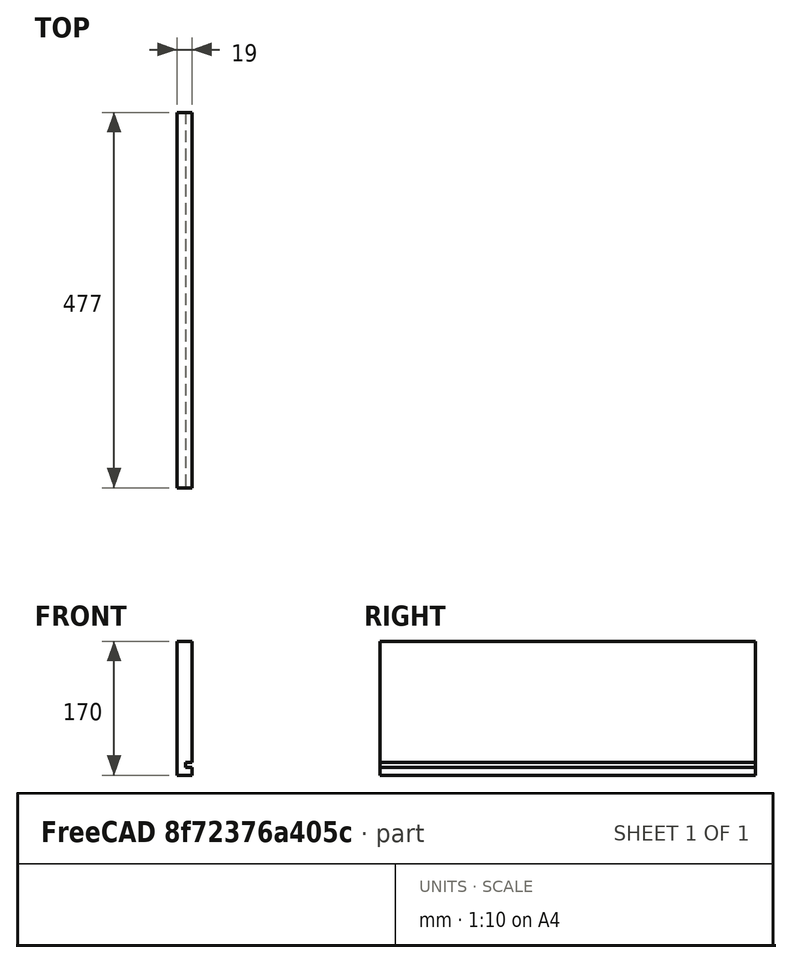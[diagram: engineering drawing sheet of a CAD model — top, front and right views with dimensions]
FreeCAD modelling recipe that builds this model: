
FCSTD DOCUMENT  (FreeCAD 1.0RUnknown)
Label: drawer_front
License: All rights reserved
objects: PartDesign::CoordinateSystem×3, Sketcher::SketchObject×1, PartDesign::Pad×1, PartDesign::Body×1
note: 9 computed .brp shape members not serialized (recipe doc carries the construction recipe); baked Part::Feature solids carry a one-line shape summary decoded from their .brp
EXTERNAL_REF file=../../mastersketch.FCStd obj=Spreadsheet

FEATURE [Sketcher::SketchObject] Sketch
  ArcFitTolerance = 1e-06
  AttachmentSupport = -> [XZ_Plane]
  FullyConstrained = true
  MakeInternals = false
  MapMode = 5
  Placement = pos=(0,0,0) rot=(1,0,0;1.5708rad)
  expr: Constraints[13] = mastersketch#Spreadsheet.drawer_outer_thickness
  expr: Constraints[19] = mastersketch#Spreadsheet.drawer_bottom_thickness + mastersketch#Spreadsheet.drawer_bottom_tol
  expr: Constraints[20] = mastersketch#Spreadsheet.drawer_slot_height
  expr: Constraints[21] = mastersketch#Spreadsheet.drawer_height
  expr: Constraints[22] = mastersketch#Spreadsheet.drawer_slot_depth
  sketch-geometry (9):
    g0: LineSegment StartX=-9.5 StartY=-85 StartZ=0 EndX=9.5 EndY=-85 EndZ=0
    g1: LineSegment StartX=9.5 StartY=-85 StartZ=0 EndX=9.5 EndY=-75 EndZ=0
    g2: LineSegment StartX=9.5 StartY=85 StartZ=0 EndX=-9.5 EndY=85 EndZ=0
    g3: LineSegment StartX=-9.5 StartY=85 StartZ=0 EndX=-9.5 EndY=-85 EndZ=0
    g4: GeomPoint [constr] X=0 Y=0 Z=0
    g5: LineSegment StartX=9.5 StartY=-68.5 StartZ=0 EndX=1.5 EndY=-68.5 EndZ=0
    g6: LineSegment StartX=1.5 StartY=-68.5 StartZ=0 EndX=1.5 EndY=-75 EndZ=0
    g7: LineSegment StartX=1.5 StartY=-75 StartZ=0 EndX=9.5 EndY=-75 EndZ=0
    g8: LineSegment StartX=9.5 StartY=-68.5 StartZ=0 EndX=9.5 EndY=85 EndZ=0
  constraints (23):
    c: Coincident(g0,g1)
    c: Coincident(g8,g2)
    c: Coincident(g2,g3)
    c: Coincident(g3,g0)
    c: Horizontal(g0)
    c: Vertical(g1)
    c: Symmetric(g2,g0,g4)
    c: Coincident(g4,g-1)
    c: Coincident(g5,g6)
    c: Coincident(g6,g7)
    c: Vertical(g6)
    c: Horizontal(g5)
    c: Horizontal(g7)
    c: DistanceX(g2,g2) = 19
    c: Parallel(g3,g8)
    c: Coincident(g5,g8)
    c: Coincident(g7,g1)
    c: Vertical(g5,g1)
    c: Symmetric(g2,g2,g-2)
    c: Distance(g5,g1) = 6.5
    c: Distance(g6,g0) = 10
    c: DistanceY(g3,g3) = 170
    c: DistanceX(g5,g5) = 8
FEATURE [PartDesign::Pad] Pad
  Direction = (0,-1,2e-16)
  Length = 477
  Length2 = 10
  Placement = pos=(0,0,0) rot=(1,0,0;1.5708rad)
  Profile = -> Sketch
  ReferenceAxis = -> Sketch [N_Axis]
  Refine = true
  Suppressed = false
  Type = 0
  expr: Length = mastersketch#Spreadsheet.drawer_width
FEATURE [PartDesign::CoordinateSystem] LCS_left
  AttacherType = Attacher::AttachEngine3D
  AttachmentSupport = -> [Pad]
  MapMode = 7
  Placement = pos=(9.5,0,85) rot=(0,1,0;3.14159rad)
FEATURE [PartDesign::CoordinateSystem] LCS_right
  AttacherType = Attacher::AttachEngine3D
  AttachmentSupport = -> [Pad]
  MapMode = 7
  Placement = pos=(9.5,-477,85) rot=(0,1,0;3.14159rad)
FEATURE [PartDesign::CoordinateSystem] LCS_bottom_center
  AttacherType = Attacher::AttachEngine3D
  AttachmentSupport = -> [Pad]
  MapMode = 45
  Placement = pos=(1.5,-238.5,-75) rot=(0,0.707107,0.707107;3.14159rad)
FEATURE [PartDesign::Body] Body  label="drawer_front"
  AllowCompound = false
  Group = -> [Sketch,Pad,LCS_left,LCS_right,LCS_bottom_center]
  Origin = -> Origin
  Tip = -> Pad
